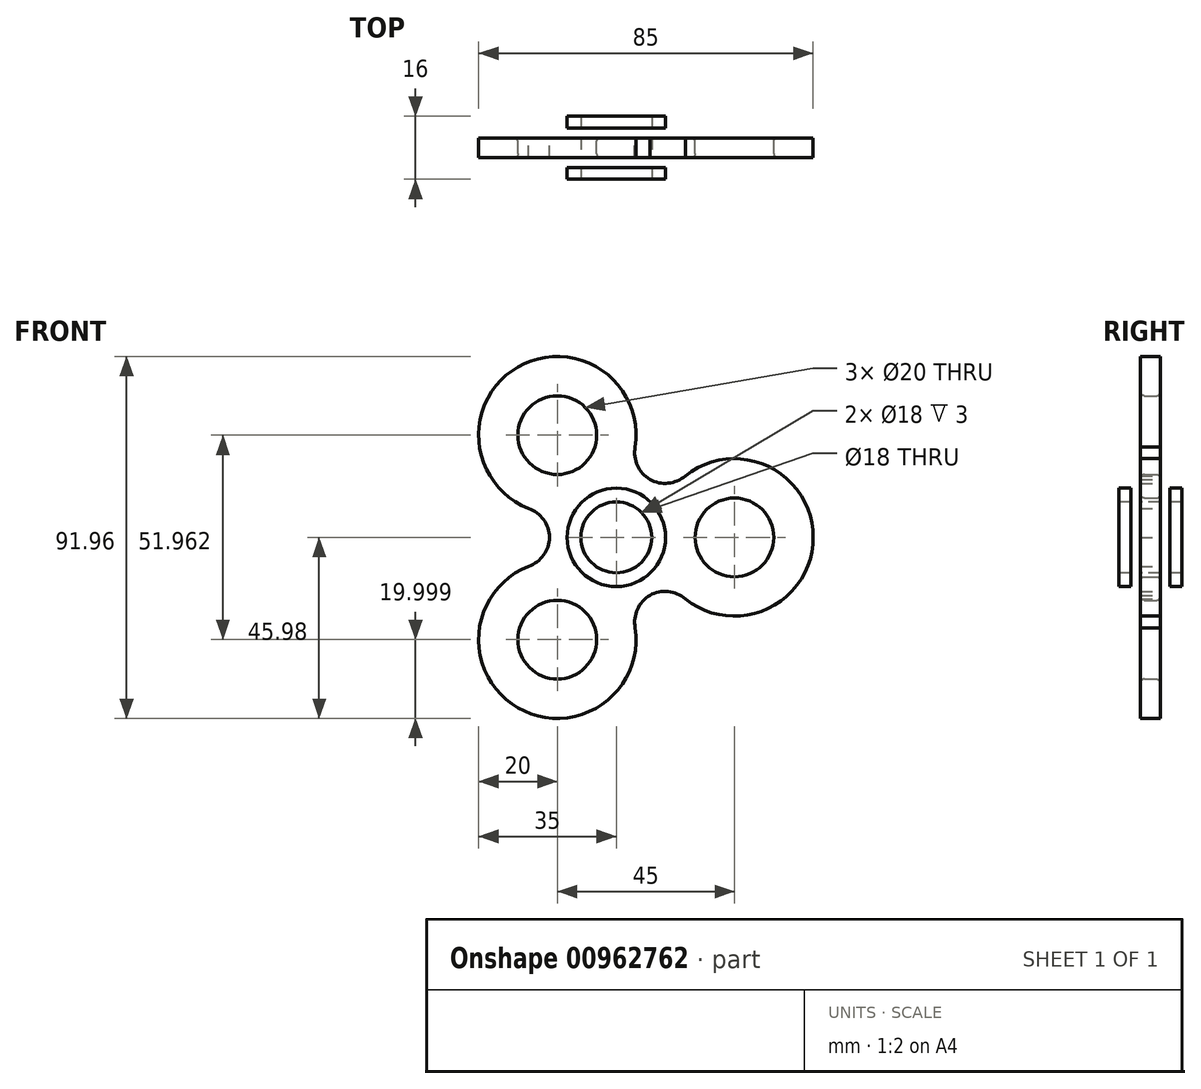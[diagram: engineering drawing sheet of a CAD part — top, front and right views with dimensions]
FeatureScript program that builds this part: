
annotation { "Feature Type Name" : "Feature", "Feature Type Description" : "" }
export const myFeature = defineFeature(function(context is Context, id is Id, definition is map)
    precondition{}
    {
        {
            var Q0;
            Q0=qCreatedBy(makeId("Front.planeOp"),FACE);
            var sketch = newSketch(context, id + "F0", { "sketchPlane" : qUnion([Q0])});
            skCircle(sketch, "E0", {"center": v(0, 0) * mm, "radius": 12.5 * mm});
            skSolve(sketch);
        }
        {
            var Q0;
            Q0=qSketchRegion(id+"F0",true);
            extrude(context, id + "F1", {"entities" : qUnion([Q0]), "depth" : 3 * mm, "offsetDistance" : 25 * mm});
        }
        {
            var Q0;
            Q0=makeQuery(id+"F1.opExtrude","CAP_FACE",FACE,{"disambiguationData":[OSD([sQuery(id+"F0.wireOp",EDGE,"E0")])],"isStart":false});
            var sketch = newSketch(context, id + "F2", { "sketchPlane" : qUnion([Q0])});
            skCircle(sketch, "E1", {"center": v(0, 0) * mm, "radius": 4 * mm});
            skCircle(sketch, "E2", {"center": v(0, 0) * mm, "radius": 5 * mm});
            skSolve(sketch);
        }
        {
            var Q0;
            Q0=qSketchRegion(id+"F2",true);
            extrude(context, id + "F3", {"entities" : qUnion([Q0]), "operationType" : NewBodyOperationType.ADD, "depth" : 2 * mm, "offsetDistance" : 25 * mm});
        }
        {
            var Q0;
            {var subQ0=sQuery(id+"F0.wireOp",EDGE,"E0");Q0=makeQuery(id+"F3.boolean.opBoolean","SPLIT",FACE,{"disambiguationData":[TD([makeQuery(id+"F1.opExtrude","SWEPT_FACE",FACE,{"disambiguationData":[OSD([subQ0])]})])],"derivedFrom":makeQuery(id+"F1.opExtrude","CAP_FACE",FACE,{"disambiguationData":[OSD([subQ0])],"isStart":false})});}
            var sketch = newSketch(context, id + "F4", { "sketchPlane" : qUnion([Q0])});
            skCircle(sketch, "E3", {"center": v(0, 0) * mm, "radius": 3 * mm});
            skSolve(sketch);
        }
        {
            var Q0;
            Q0=qSketchRegion(id+"F4",true);
            extrude(context, id + "F5", {"entities" : qUnion([Q0]), "operationType" : NewBodyOperationType.ADD, "depth" : 10 * mm, "offsetDistance" : 25 * mm});
        }
        {
            var Q0;
            {var subQ0=sQuery(id+"F0.wireOp",EDGE,"E0");Q0=makeQuery(id+"F3.boolean.opBoolean","SPLIT",FACE,{"disambiguationData":[TD([makeQuery(id+"F1.opExtrude","SWEPT_FACE",FACE,{"disambiguationData":[OSD([subQ0])]})])],"derivedFrom":makeQuery(id+"F1.opExtrude","CAP_FACE",FACE,{"disambiguationData":[OSD([subQ0])],"isStart":false})});}
            cPlane(context, id + "F6", {"entities" : qUnion([Q0]), "cplaneType" : CPlaneType.OFFSET, "offset" : 0 * mm, "oppositeDirection" : true, "width" : 150 * mm, "height" : 150 * mm});
        }
        {
            var Q0;
            Q0=qCreatedBy(id+"F6.planeOp",FACE);
            var sketch = newSketch(context, id + "F7", { "sketchPlane" : qUnion([Q0])});
            skCircle(sketch, "E4", {"center": v(0, 0) * mm, "radius": 5 * mm});
            skCircle(sketch, "E5", {"center": v(0, 0) * mm, "radius": 6 * mm});
            skSolve(sketch);
        }
        {
            var Q0;
            Q0=qSketchRegion(id+"F7",true);
            extrude(context, id + "F8", {"entities" : qUnion([Q0]), "depth" : 10 * mm, "offsetDistance" : 25 * mm});
        }
        {
            var Q0;
            Q0=qCreatedBy(id+"F6.planeOp",FACE);
            var sketch = newSketch(context, id + "F9", { "sketchPlane" : qUnion([Q0])});
            skCircle(sketch, "E6", {"center": v(0, 0) * mm, "radius": 8 * mm});
            skCircle(sketch, "E7", {"center": v(0, 0) * mm, "radius": 9 * mm});
            skSolve(sketch);
        }
        {
            var Q0;
            Q0=qSketchRegion(id+"F9",true);
            extrude(context, id + "F10", {"entities" : qUnion([Q0]), "depth" : 10 * mm, "offsetDistance" : 25 * mm});
        }
        {
            var Q0;
            Q0=makeQuery(id+"F5.opExtrude","CAP_FACE",FACE,{"disambiguationData":[OSD([sQuery(id+"F4.wireOp",EDGE,"E3")])],"isStart":false});
            cPlane(context, id + "F11", {"entities" : qUnion([Q0]), "cplaneType" : CPlaneType.OFFSET, "offset" : 0 * mm, "width" : 150 * mm, "height" : 150 * mm});
        }
        {
            var Q0;
            Q0=qCreatedBy(id+"F11.planeOp",FACE);
            var sketch = newSketch(context, id + "F12", { "sketchPlane" : qUnion([Q0])});
            skCircle(sketch, "E8", {"center": v(0, 0) * mm, "radius": 12.5 * mm});
            skSolve(sketch);
        }
        {
            var Q0;
            Q0=qSketchRegion(id+"F12",true);
            extrude(context, id + "F13", {"entities" : qUnion([Q0]), "operationType" : NewBodyOperationType.ADD, "depth" : 3 * mm, "offsetDistance" : 25 * mm});
        }
        {
            var Q0;
            Q0=qCreatedBy(id+"F11.planeOp",FACE);
            var sketch = newSketch(context, id + "F14", { "sketchPlane" : qUnion([Q0])});
            skCircle(sketch, "E9", {"center": v(0, 0) * mm, "radius": 4 * mm});
            skCircle(sketch, "E10", {"center": v(0, 0) * mm, "radius": 3 * mm});
            skSolve(sketch);
        }
        {
            var Q0;
            Q0=qSketchRegion(id+"F14",true);
            extrude(context, id + "F15", {"entities" : qUnion([Q0]), "operationType" : NewBodyOperationType.ADD, "oppositeDirection" : true, "depth" : 3 * mm, "offsetDistance" : 25 * mm});
        }
        {
            var Q0;
            Q0=qCreatedBy(id+"F6.planeOp",FACE);
            cPlane(context, id + "F16", {"entities" : qUnion([Q0]), "cplaneType" : CPlaneType.OFFSET, "offset" : 5 * mm, "width" : 150 * mm, "height" : 150 * mm});
        }
        {
            var Q0;
            Q0=qCreatedBy(id+"F16.planeOp",FACE);
            var sketch = newSketch(context, id + "F17", { "sketchPlane" : qUnion([Q0])});
            skLineSegment(sketch, "E11", {"start": v(0, 0) * mm, "end": v(30, 0) * mm, "construction": true});
            skLineSegment(sketch, "E12", {"start": v(0, 0) * mm, "end": v(8.5, 14.71) * mm});
            skArc(sketch, "E13", {"start": v(8.5, 14.71) * mm, "mid": v(13.15, 13.77) * mm, "end": v(17.53, 15.63) * mm});
            skArc(sketch, "E14.MirrorCS", {"start": v(8.5, -14.71) * mm, "mid": v(13.15, -13.77) * mm, "end": v(17.53, -15.63) * mm});
            skLineSegment(sketch, "E15.MirrorCS", {"start": v(0, 0) * mm, "end": v(8.5, -14.71) * mm});
            skArc(sketch, "E16", {"start": v(17.53, 15.63) * mm, "mid": v(50, 0) * mm, "end": v(17.53, -15.63) * mm});
            skCircle(sketch, "E17", {"center": v(30, 0) * mm, "radius": 10 * mm});
            skSolve(sketch);
        }
        {
            var Q0;
            Q0=qSketchRegion(id+"F17",true);
            extrude(context, id + "F18", {"entities" : qUnion([Q0]), "endBound" : BoundingType.SYMMETRIC, "depth" : 5 * mm, "offsetDistance" : 25 * mm});
        }
        {
            var Q0;
            Q0=makeQuery(id+"F18.opExtrude","CAP_EDGE",EDGE,{"disambiguationData":[OSD([sQuery(id+"F17.wireOp",EDGE,"E17")])],"isStart":false});
            var Q1;
            Q1=makeQuery(id+"F18.opExtrude","CAP_EDGE",EDGE,{"disambiguationData":[OSD([sQuery(id+"F17.wireOp",EDGE,"E17")])],"isStart":true});
            fillet(context, id + "F19", {"entities" : qUnion([Q0, Q1]), "radius" : 1 * mm, "tangentPropagation" : true, "allowEdgeOverflow" : false});
        }
        {
            var Q0;
            Q0=makeQuery(id+"F18.opExtrude","SWEPT_BODY",BODY,{"disambiguationData":[OSD([sQuery(id+"F17.wireOp",EDGE,"E12"),sQuery(id+"F17.wireOp",EDGE,"E13"),sQuery(id+"F17.wireOp",EDGE,"E14.MirrorCS"),sQuery(id+"F17.wireOp",EDGE,"E15.MirrorCS"),sQuery(id+"F17.wireOp",EDGE,"E16"),sQuery(id+"F17.wireOp",EDGE,"E17")])]});
            var Q1;
            Q1=makeQuery(id+"F10.opExtrude","SWEPT_FACE",FACE,{"disambiguationData":[OSD([sQuery(id+"F9.wireOp",EDGE,"E7")])]});
            circularPattern(context, id + "F20", {"operationType" : NewBodyOperationType.ADD, "entities" : qUnion([Q0]), "axis" : qUnion([Q1]), "angle" : 360 * degree, "instanceCount" : 3, "equalSpace" : true});
        }
        {
            var Q0;
            Q0=qCreatedBy(id+"F16.planeOp",FACE);
            var sketch = newSketch(context, id + "F21", { "sketchPlane" : qUnion([Q0])});
            skCircle(sketch, "E18.0.0", {"center": v(0, 0) * mm, "radius": 9 * mm});
            skSolve(sketch);
        }
        {
            var Q0;
            Q0=qSketchRegion(id+"F21",true);
            extrude(context, id + "F22", {"entities" : qUnion([Q0]), "operationType" : NewBodyOperationType.REMOVE, "endBound" : BoundingType.SYMMETRIC, "oppositeDirection" : true, "depth" : 25 * mm, "offsetDistance" : 25 * mm});
        }
    });
